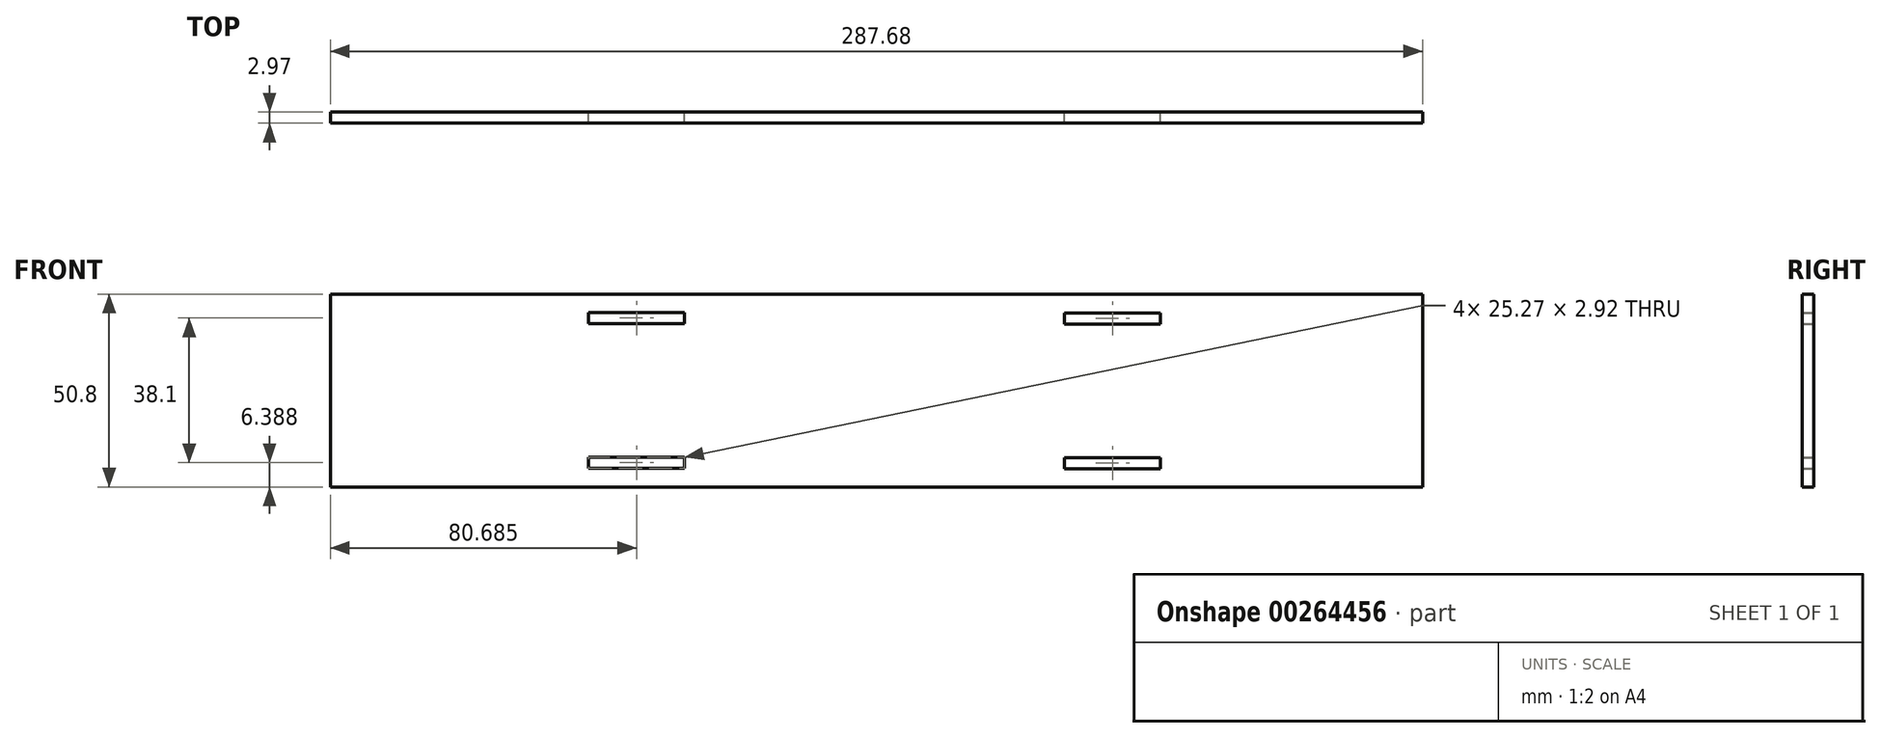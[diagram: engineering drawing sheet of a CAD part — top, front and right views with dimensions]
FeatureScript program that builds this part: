
annotation { "Feature Type Name" : "Feature", "Feature Type Description" : "" }
export const myFeature = defineFeature(function(context is Context, id is Id, definition is map)
    precondition{}
    {
        {
            var Q0;
            Q0=qCreatedBy(makeId("Front.planeOp"),FACE);
            var sketch = newSketch(context, id + "F0", { "sketchPlane" : qUnion([Q0])});
            skLineSegment(sketch, "E0", {"start": v(-145.7, -25.4) * mm, "end": v(141.97, -25.4) * mm});
            skLineSegment(sketch, "E1", {"start": v(-77.66, -17.55) * mm, "end": v(-52.39, -17.55) * mm});
            skLineSegment(sketch, "E2", {"start": v(47.69, -17.63) * mm, "end": v(72.96, -17.63) * mm});
            skLineSegment(sketch, "E3.MirrorCS", {"start": v(-77.66, -20.47) * mm, "end": v(-52.39, -20.47) * mm});
            skLineSegment(sketch, "E4.MirrorCS", {"start": v(-77.66, 17.63) * mm, "end": v(-52.39, 17.63) * mm});
            skLineSegment(sketch, "E5.MirrorCS", {"start": v(-77.66, 20.55) * mm, "end": v(-52.39, 20.55) * mm});
            skLineSegment(sketch, "E6.MirrorCS", {"start": v(-145.7, 25.4) * mm, "end": v(141.97, 25.4) * mm});
            skLineSegment(sketch, "E7.MirrorCS", {"start": v(47.69, 20.47) * mm, "end": v(72.96, 20.47) * mm});
            skLineSegment(sketch, "E8.MirrorCS", {"start": v(47.69, 17.55) * mm, "end": v(72.96, 17.55) * mm});
            skLineSegment(sketch, "E9", {"start": v(-52.39, -17.55) * mm, "end": v(-52.39, -20.47) * mm});
            skLineSegment(sketch, "E10", {"start": v(-77.66, -17.55) * mm, "end": v(-77.66, -20.47) * mm});
            skLineSegment(sketch, "E11", {"start": v(-52.39, 20.55) * mm, "end": v(-52.39, 17.63) * mm});
            skLineSegment(sketch, "E12", {"start": v(-77.66, 20.55) * mm, "end": v(-77.66, 17.63) * mm});
            skLineSegment(sketch, "E13", {"start": v(72.96, 20.47) * mm, "end": v(72.96, 17.55) * mm});
            skLineSegment(sketch, "E14", {"start": v(47.69, 20.47) * mm, "end": v(47.69, 17.55) * mm});
            skLineSegment(sketch, "E15", {"start": v(72.96, -20.55) * mm, "end": v(47.69, -20.55) * mm});
            skLineSegment(sketch, "E16", {"start": v(47.69, -17.63) * mm, "end": v(47.69, -20.55) * mm});
            skLineSegment(sketch, "E17", {"start": v(-145.7, 25.4) * mm, "end": v(-145.7, -25.4) * mm});
            skLineSegment(sketch, "E18", {"start": v(141.97, 25.4) * mm, "end": v(141.97, -25.4) * mm});
            skLineSegment(sketch, "E19", {"start": v(72.96, -17.63) * mm, "end": v(72.96, -20.55) * mm});
            skSolve(sketch);
        }
        {
            var Q0;
            Q0=makeQuery(id+"F0.imprint","IMPRINT",FACE,{"disambiguationData":[TD([[makeQuery(id+"F0.imprint","IMPRINT",EDGE,{"derivedFrom":sQuery(id+"F0.wireOp",EDGE,"E0")}),1.0]])]});
            extrude(context, id + "F1", {"entities" : qUnion([Q0]), "depth" : 2.97 * mm});
        }
    });
